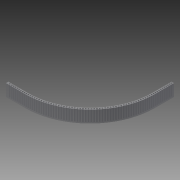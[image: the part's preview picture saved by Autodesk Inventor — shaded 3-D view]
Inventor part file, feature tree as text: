
AUTODESK INVENTOR PART (.ipt)
format: ipt  version: 2013 (Build 170138000, 138)  size: 194,560 bytes
history: native  units: in
note: dims shown in document units (in); Inventor stores cm internally (conversion verified against a paired STEP export)
features: extrude x1, sketch x1
ambient origin geometry x8: Origin, YZ Plane, XZ Plane, XY Plane, X Axis, Y Axis, Z Axis, Center Point
bodies: Solid1 (feature_tree)
feature tree (2):
  extrude  "Extrusion1"  Depth=27.0in
  sketch  "Sketch1"  dims[d0=26.0in d1=27.0in d2=4.0in d3=4.3307in d5=0.375in d6=0.3937in d8=1.0in d10=4.0in d11=9.8425in d13=0.2907in d15=9.8425in d17=0.2907in d19=3.5433in d21=0.375in d22=0.3937in d24=1.0in d26=2.5in d27=0.0in]
